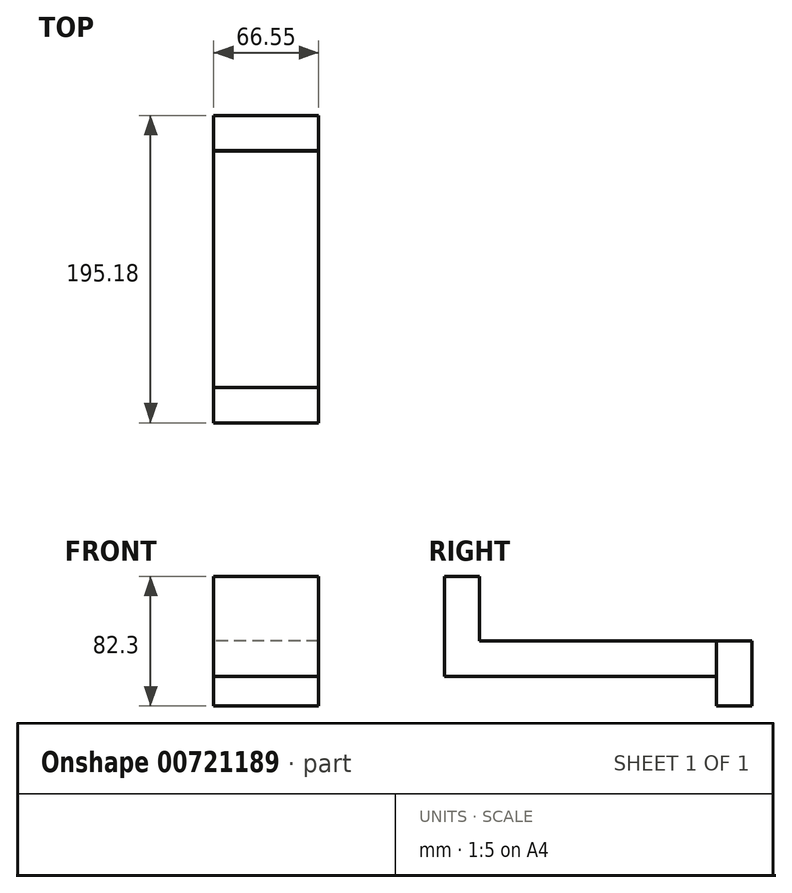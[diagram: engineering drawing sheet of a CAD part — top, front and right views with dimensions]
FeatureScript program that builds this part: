
annotation { "Feature Type Name" : "Feature", "Feature Type Description" : "" }
export const myFeature = defineFeature(function(context is Context, id is Id, definition is map)
    precondition{}
    {
        {
            var Q0;
            Q0=qCreatedBy(makeId("Right.planeOp"),FACE);
            var sketch = newSketch(context, id + "F0", { "sketchPlane" : qUnion([Q0])});
            skLineSegment(sketch, "E0.bottom", {"start": v(-71.5, 41.15) * mm, "end": v(-49.15, 41.15) * mm});
            skLineSegment(sketch, "E0.top", {"start": v(-71.5, -22.35) * mm, "end": v(-49.15, -22.35) * mm});
            skLineSegment(sketch, "E0.left", {"start": v(-71.5, 41.15) * mm, "end": v(-71.5, -22.35) * mm});
            skLineSegment(sketch, "E0.right", {"start": v(-49.15, 41.15) * mm, "end": v(-49.15, -22.35) * mm});
            skLineSegment(sketch, "E1.bottom", {"start": v(-49.15, -22.35) * mm, "end": v(101.22, -22.35) * mm});
            skLineSegment(sketch, "E1.top", {"start": v(-49.15, 0) * mm, "end": v(101.33, 0) * mm});
            skLineSegment(sketch, "E1.left", {"start": v(-49.15, -22.35) * mm, "end": v(-49.15, 0) * mm});
            skLineSegment(sketch, "E2.top", {"start": v(101.33, 0) * mm, "end": v(101.22, 0) * mm});
            skLineSegment(sketch, "E3", {"start": v(101.22, 0) * mm, "end": v(101.22, -22.35) * mm});
            skLineSegment(sketch, "E4.bottom", {"start": v(103.63, 0) * mm, "end": v(101.33, 0) * mm});
            skLineSegment(sketch, "E4.top", {"start": v(103.63, 0) * mm, "end": v(101.33, 0) * mm});
            skLineSegment(sketch, "E4.left", {"start": v(103.63, 0) * mm, "end": v(103.63, 0) * mm});
            skLineSegment(sketch, "E4.right", {"start": v(101.33, 0) * mm, "end": v(101.33, 0) * mm});
            skLineSegment(sketch, "E5.bottom", {"start": v(101.33, 0) * mm, "end": v(123.68, 0) * mm});
            skLineSegment(sketch, "E5.top", {"start": v(101.33, -41.15) * mm, "end": v(123.68, -41.15) * mm});
            skLineSegment(sketch, "E5.left", {"start": v(101.33, 0) * mm, "end": v(101.33, -41.15) * mm});
            skLineSegment(sketch, "E5.right", {"start": v(123.68, 0) * mm, "end": v(123.68, -41.15) * mm});
            skSolve(sketch);
        }
        {
            var Q0;
            Q0=makeQuery(id+"F0.imprint","IMPRINT",FACE,{"disambiguationData":[TD([[makeQuery(id+"F0.imprint","IMPRINT",EDGE,{"derivedFrom":sQuery(id+"F0.wireOp",EDGE,"E1.bottom")}),1.0]])]});
            var Q1;
            Q1=makeQuery(id+"F0.imprint","IMPRINT",FACE,{"disambiguationData":[TD([[makeQuery(id+"F0.imprint","IMPRINT",EDGE,{"derivedFrom":sQuery(id+"F0.wireOp",EDGE,"E0.bottom")}),-1.0]])]});
            var Q2;
            Q2=makeQuery(id+"F0.imprint","IMPRINT",FACE,{"disambiguationData":[TD([[makeQuery(id+"F0.imprint","IMPRINT",EDGE,{"derivedFrom":sQuery(id+"F0.wireOp",EDGE,"E5.top")}),1.0]])]});
            extrude(context, id + "F1", {"entities" : qUnion([Q0, Q1, Q2]), "depth" : 66.55 * mm, "offsetDistance" : 25.4 * mm});
        }
    });
